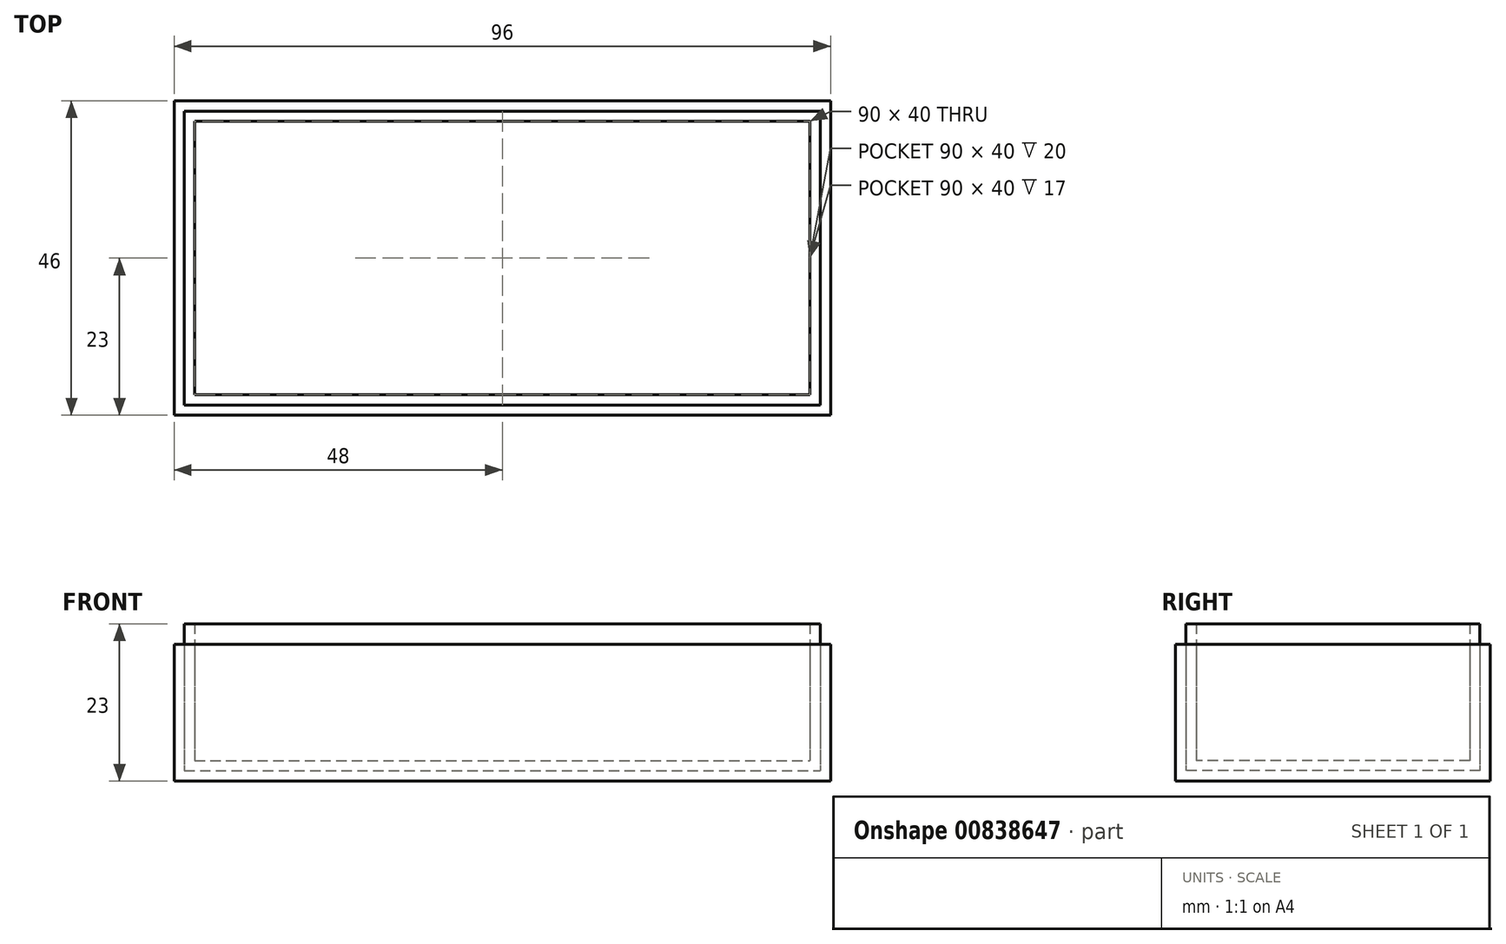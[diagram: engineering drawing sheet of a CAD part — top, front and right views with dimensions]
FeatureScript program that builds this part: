
annotation { "Feature Type Name" : "Feature", "Feature Type Description" : "" }
export const myFeature = defineFeature(function(context is Context, id is Id, definition is map)
    precondition{}
    {
        {
            var Q0;
            Q0=qCreatedBy(makeId("Top.planeOp"),FACE);
            var sketch = newSketch(context, id + "F0", { "sketchPlane" : qUnion([Q0])});
            skLineSegment(sketch, "E0.bottom", {"start": v(-45, 20) * mm, "end": v(45, 20) * mm});
            skLineSegment(sketch, "E0.top", {"start": v(-45, -20) * mm, "end": v(45, -20) * mm});
            skLineSegment(sketch, "E0.left", {"start": v(-45, 20) * mm, "end": v(-45, -20) * mm});
            skLineSegment(sketch, "E0.right", {"start": v(45, 20) * mm, "end": v(45, -20) * mm});
            skSolve(sketch);
        }
        {
            var Q0;
            Q0=makeQuery(id+"F0.imprint","IMPRINT",FACE,{"disambiguationData":[TD([[makeQuery(id+"F0.imprint","IMPRINT",EDGE,{"derivedFrom":sQuery(id+"F0.wireOp",EDGE,"E0.bottom")}),-1.0]])]});
            extrude(context, id + "F1", {"entities" : qUnion([Q0]), "depth" : 17 * mm, "offsetDistance" : 25 * mm});
        }
        {
            var Q0;
            Q0=makeQuery(id+"F1.opExtrude","CAP_FACE",FACE,{"disambiguationData":[OSD([sQuery(id+"F0.wireOp",EDGE,"E0.bottom"),sQuery(id+"F0.wireOp",EDGE,"E0.top"),sQuery(id+"F0.wireOp",EDGE,"E0.left"),sQuery(id+"F0.wireOp",EDGE,"E0.right")])],"isStart":false});
            shell(context, id + "F2", {"entities" : qUnion([Q0]), "thickness" : 3 * mm, "oppositeDirection" : true});
        }
        {
            var Q0;
            Q0=makeQuery(id+"F2.opShell","OFFSET_FACE",FACE,{"disambiguationData":[OSD([sQuery(id+"F0.wireOp",EDGE,"E0.bottom"),sQuery(id+"F0.wireOp",EDGE,"E0.top"),sQuery(id+"F0.wireOp",EDGE,"E0.left"),sQuery(id+"F0.wireOp",EDGE,"E0.right")])]});
            extrude(context, id + "F3", {"entities" : qUnion([Q0]), "depth" : 20 * mm, "offsetDistance" : 25 * mm});
        }
        {
            var Q0;
            Q0=makeQuery(id+"F3.opExtrude","CAP_FACE",FACE,{"disambiguationData":[OSD([sQuery(id+"F0.wireOp",EDGE,"E0.bottom"),sQuery(id+"F0.wireOp",EDGE,"E0.top"),sQuery(id+"F0.wireOp",EDGE,"E0.left"),sQuery(id+"F0.wireOp",EDGE,"E0.right")])],"isStart":false});
            shell(context, id + "F4", {"entities" : qUnion([Q0]), "thickness" : 1.5 * mm, "oppositeDirection" : true});
        }
    });
